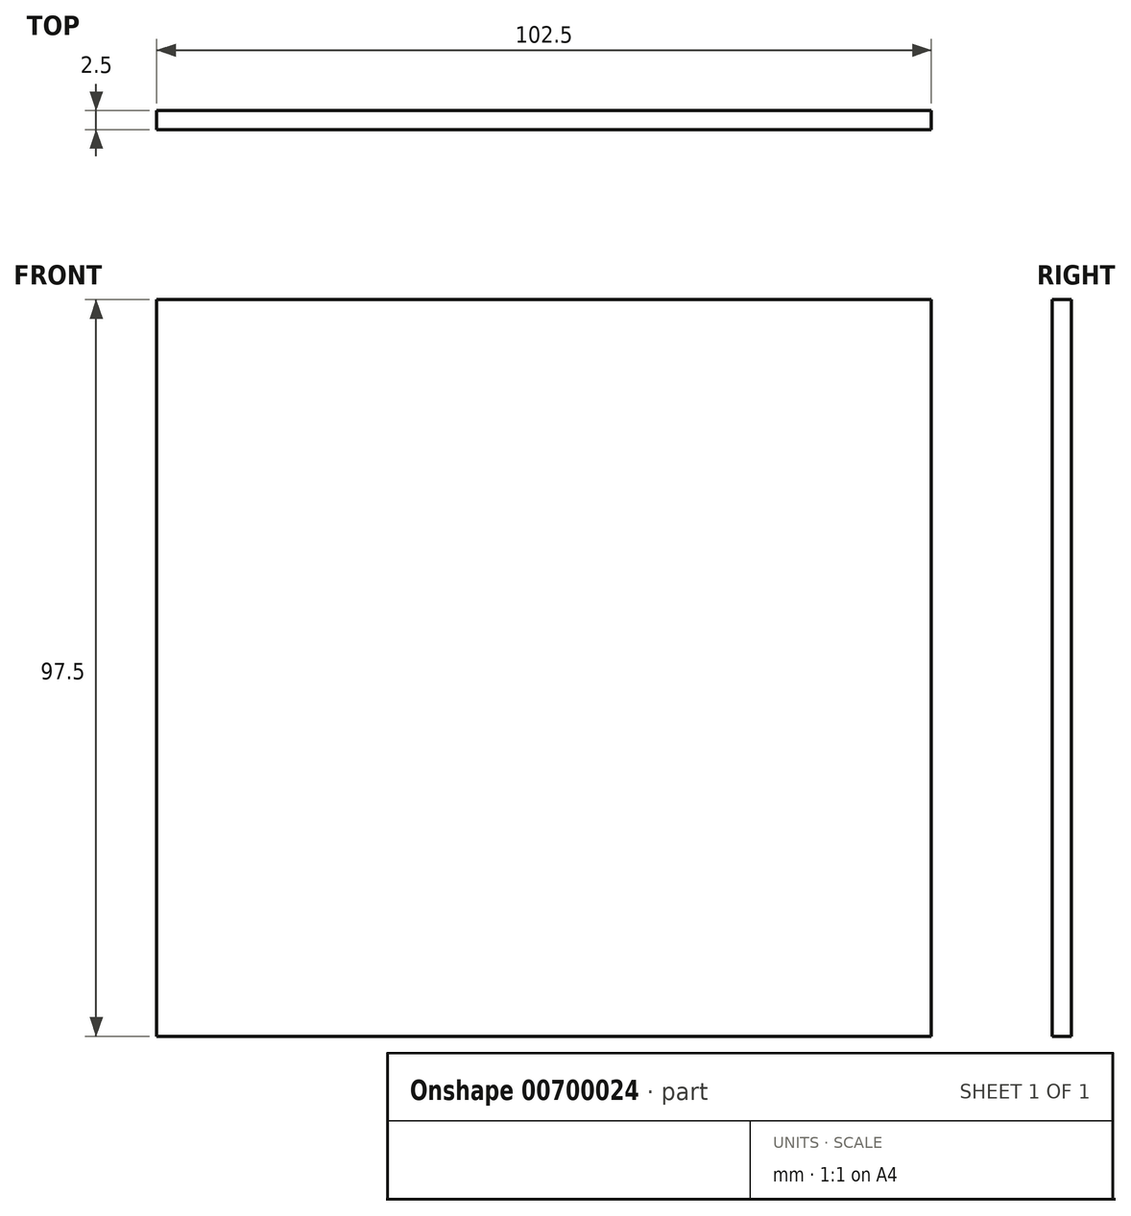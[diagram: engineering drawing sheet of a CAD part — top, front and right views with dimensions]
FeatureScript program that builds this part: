
annotation { "Feature Type Name" : "Feature", "Feature Type Description" : "" }
export const myFeature = defineFeature(function(context is Context, id is Id, definition is map)
    precondition{}
    {
        {
            var Q0;
            Q0=qCreatedBy(makeId("Front.planeOp"),FACE);
            var sketch = newSketch(context, id + "F0", { "sketchPlane" : qUnion([Q0])});
            skLineSegment(sketch, "E0.bottom", {"start": v(51.25, -48.75) * mm, "end": v(-51.25, -48.75) * mm});
            skLineSegment(sketch, "E0.top", {"start": v(51.25, 48.75) * mm, "end": v(-51.25, 48.75) * mm});
            skLineSegment(sketch, "E0.left", {"start": v(51.25, -48.75) * mm, "end": v(51.25, 48.75) * mm});
            skLineSegment(sketch, "E0.right", {"start": v(-51.25, -48.75) * mm, "end": v(-51.25, 48.75) * mm});
            skPoint(sketch, "E0.middle", {"position": v(0, 0) * mm});
            skSolve(sketch);
        }
        {
            var Q0;
            Q0=qSketchRegion(id+"F0",true);
            extrude(context, id + "F1", {"entities" : qUnion([Q0]), "depth" : 2.5 * mm, "offsetDistance" : 25 * mm});
        }
    });
